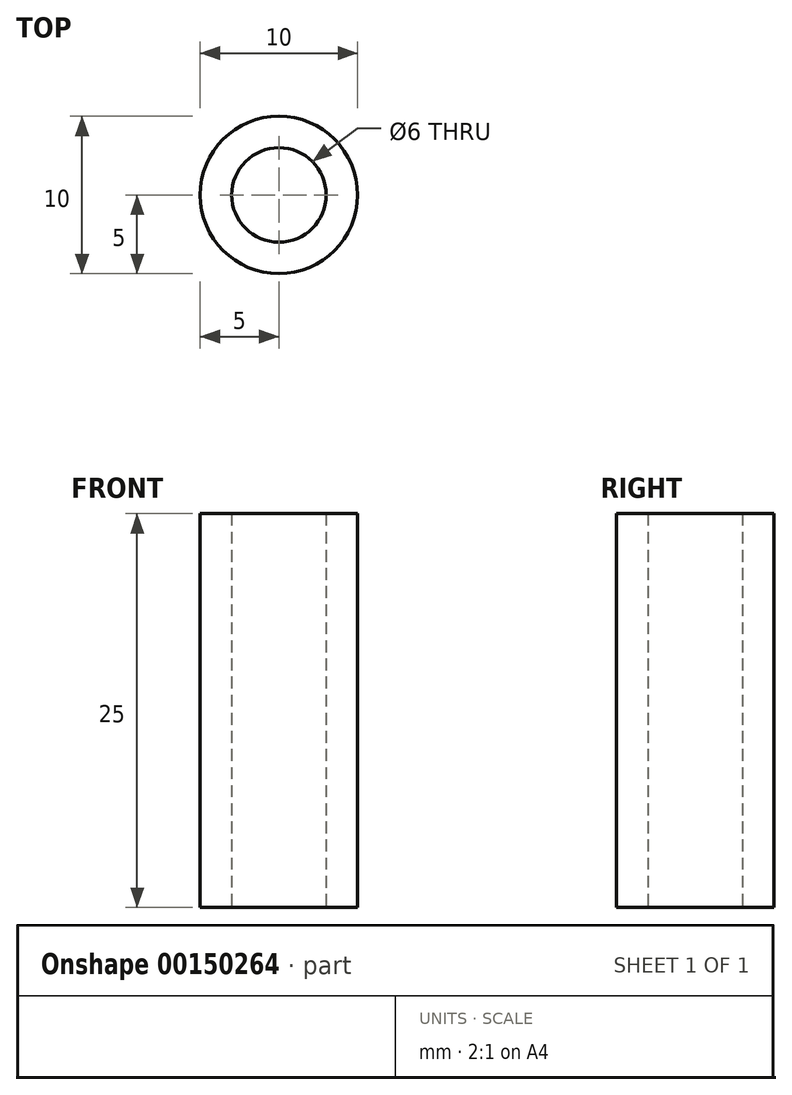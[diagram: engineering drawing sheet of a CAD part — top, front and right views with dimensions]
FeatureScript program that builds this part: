
annotation { "Feature Type Name" : "Feature", "Feature Type Description" : "" }
export const myFeature = defineFeature(function(context is Context, id is Id, definition is map)
    precondition{}
    {
        {
            var Q0;
            Q0=qCreatedBy(makeId("Top.planeOp"),FACE);
            var sketch = newSketch(context, id + "F0", { "sketchPlane" : qUnion([Q0])});
            skCircle(sketch, "E0", {"center": v(0, 0) * mm, "radius": 5 * mm});
            skCircle(sketch, "E1", {"center": v(0, 0) * mm, "radius": 3 * mm});
            skSolve(sketch);
        }
        {
            var Q0;
            Q0=makeQuery(id+"F0.imprint","IMPRINT",FACE,{"disambiguationData":[TD([[makeQuery(id+"F0.imprint","IMPRINT",EDGE,{"derivedFrom":sQuery(id+"F0.wireOp",EDGE,"E0")}),1.0]])]});
            extrude(context, id + "F1", {"entities" : qUnion([Q0]), "depth" : 25 * mm});
        }
    });
